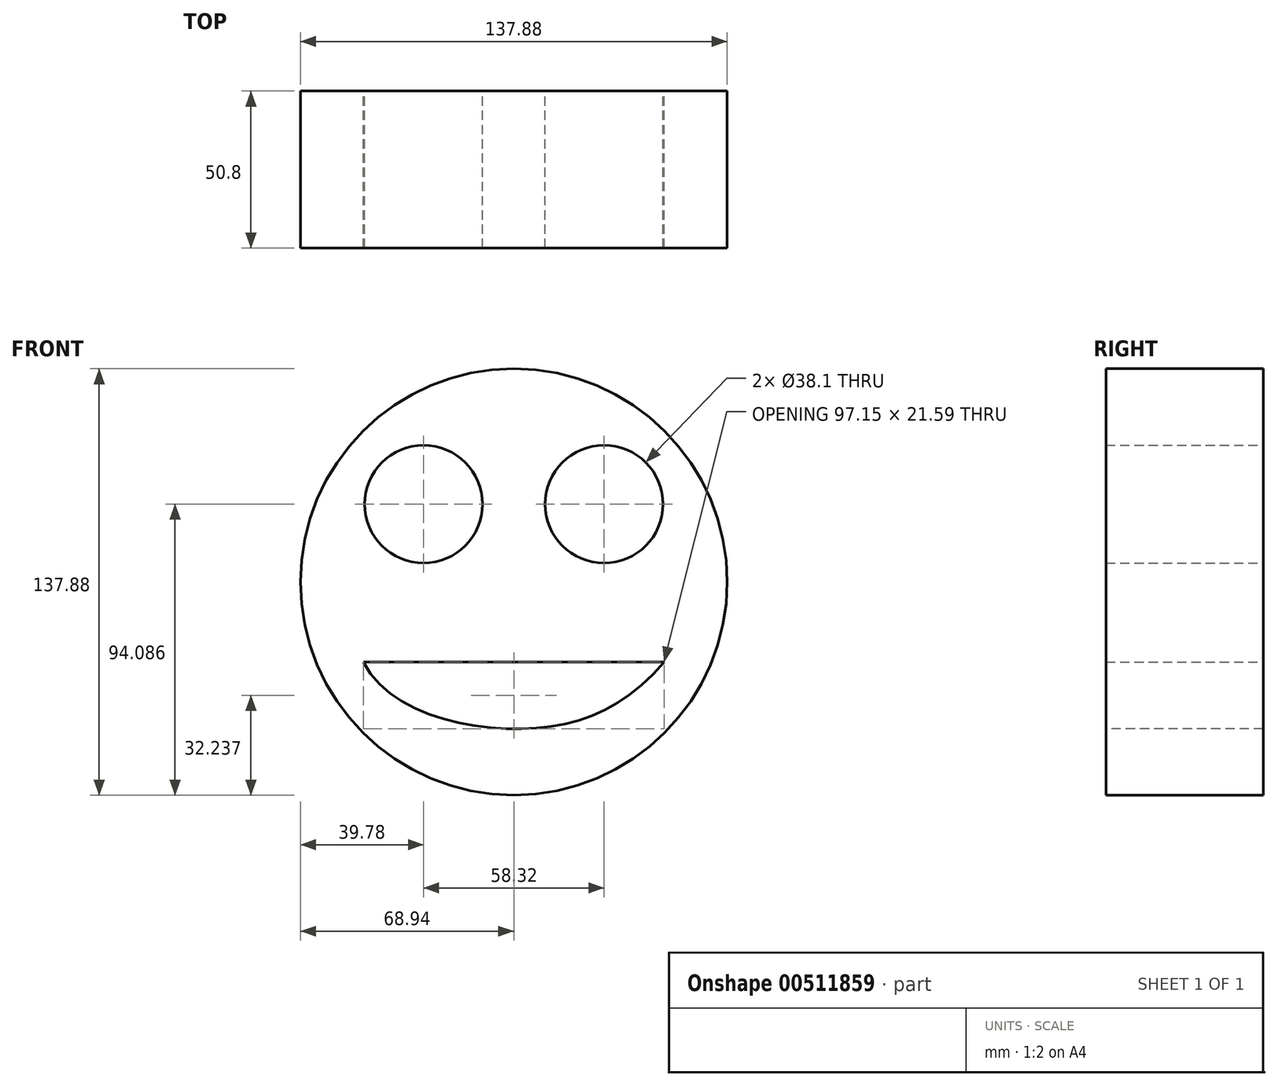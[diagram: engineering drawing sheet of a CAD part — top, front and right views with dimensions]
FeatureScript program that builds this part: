
annotation { "Feature Type Name" : "Feature", "Feature Type Description" : "" }
export const myFeature = defineFeature(function(context is Context, id is Id, definition is map)
    precondition{}
    {
        {
            var Q0;
            Q0=qCreatedBy(makeId("Front.planeOp"),FACE);
            var sketch = newSketch(context, id + "F0", { "sketchPlane" : qUnion([Q0])});
            skCircle(sketch, "E0", {"center": v(0, 0) * mm, "radius": 68.94 * mm});
            skCircle(sketch, "E1", {"center": v(-29.16, 25.15) * mm, "radius": 19.05 * mm});
            skLineSegment(sketch, "E2", {"start": v(-48.58, -25.9) * mm, "end": v(0, -25.9) * mm});
            skCircle(sketch, "E3.MirrorC", {"center": v(29.16, 25.15) * mm, "radius": 19.05 * mm});
            skLineSegment(sketch, "E4.MirrorCS", {"start": v(48.58, -25.9) * mm, "end": v(0, -25.9) * mm});
            skFitSpline(sketch, "E5", {"points": [v(-48.58, -25.9) * mm, v(0, -47.5) * mm, v(48.58, -25.9) * mm], "startDerivative": vector(46.03, -91) * mm, "endDerivative": vector(82.5, 96.75) * mm});
            skSolve(sketch);
        }
        {
            var Q0;
            Q0=makeQuery(id+"F0.imprint","IMPRINT",FACE,{"disambiguationData":[TD([[makeQuery(id+"F0.imprint","IMPRINT",EDGE,{"derivedFrom":sQuery(id+"F0.wireOp",EDGE,"E0")}),1.0]])]});
            extrude(context, id + "F1", {"entities" : qUnion([Q0]), "endBound" : BoundingType.SYMMETRIC, "depth" : 50.8 * mm});
        }
    });
